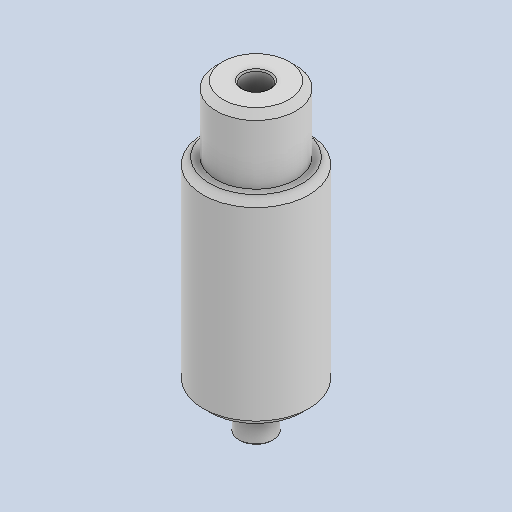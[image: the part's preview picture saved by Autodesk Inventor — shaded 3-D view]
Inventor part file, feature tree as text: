
AUTODESK INVENTOR PART (.ipt)
format: ipt  version: 2025 (Build 290162010, 162A)  size: 133,120 bytes
history: native  units: mm
features: chamfer x2, revolve x1, sketch x1
ambient origin geometry x8: Origin, YZ Plane, XZ Plane, XY Plane, X Axis, Y Axis, Z Axis, Center Point
bodies: Solid1 (feature_tree)
feature tree (4):
  revolve  "Revolution1"  [1 undecoded]
  chamfer  "Chamfer1"  Distance=15.0mm
  chamfer  "Chamfer2"  Distance=2.0mm
  sketch  "Sketch1"  dims[d0=1.0mm d1=1.3mm d3=15.0mm d4=2.0mm d5=5.0mm d6=4.0mm d7=0.8mm d8=2.0mm d9=5.0mm d10=90.0deg d11=0.5mm d12=2.0mm d13=45.0deg d14=0.1mm d15=2.0mm d16=45.0deg]
note: 1 required parameter value undecoded (feature->parameter linkage not recoverable at this tier; creation-order binding heuristic only, values carry confidence <= 0.55)
